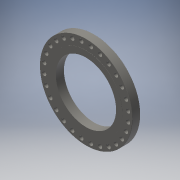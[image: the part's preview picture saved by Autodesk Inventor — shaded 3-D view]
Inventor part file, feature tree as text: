
AUTODESK INVENTOR PART (.ipt)
format: ipt  version: 2017 SP1 (Build 210196100, 196)  size: 296,960 bytes
history: native  units: in
note: dims shown in document units (in); Inventor stores cm internally (conversion verified against a paired STEP export)
features: sketch x6, extrude x4, chamfer x3, hole x2, pattern_circular x2, fillet x1, plane x1, projected_geometry x1
ambient origin geometry x8: Origin, YZ Plane, XZ Plane, XY Plane, X Axis, Y Axis, Z Axis, Center Point
bodies: Solid1 (feature_tree)
feature tree (20):
  extrude  "Extrusion: OD"  Depth=3.6875in TaperAngle=0.0deg
  extrude  "Extrusion: RF"  Depth=0.0625in TaperAngle=0.0deg
  extrude  "Extrusion: ID Large"  Depth=2.0in TaperAngle=0.0deg
  extrude  "Extrusion: ID Small"  Depth=2.0in TaperAngle=0.0deg
  hole  "Hole: Bolt"  [1 undecoded]
  chamfer  "Chamfer: Bolt hole"  Distance=11.0236in Angle=360.0deg
  pattern_circular  "Circular Pattern: Bolt hole"  Angle=45.0deg  [1 undecoded]
  chamfer  "Chamfer: OD"  Distance=0.0312in Angle=45.0deg
  chamfer  "Chamfer2"  Distance=0.0312in
  fillet  "Fillet2"  Radius=0.25in
  plane  "Work Plane1"
  hole  "Hole2"  [1 undecoded]
  pattern_circular  "Circular Pattern2"  [2 undecoded]
  sketch  "Sketch1"  dims[d0=43.0in d1=3.6875in d2=0.0in]
  sketch  "Sketch2"  dims[d3=33.75in d4=0.0625in d5=0.0in]
  sketch  "Sketch3"  dims[d6=30.0in d7=2.0in d8=0.0in]
  sketch  "Sketch4"  dims[d9=28.0in d10=2.0in d11=0.0in]
  sketch  "Sketch5"  dims[d12=39.25in d13=0.0442in]
  sketch  "Sketch6"  dims[d14=1.875in d15=0.75in d16=0.375in d17=0.25in d18=0.5635in d19=1.0in d20=0.8108in d21=11.0236in d22=360.0deg d24=0.0625in d25=0.125in d26=45.0deg d28=0.0312in d29=0.125in d30=45.0deg d31=0.0312in d32=0.25in d33=0.0625in d34=0.125in d35=45.0deg d36=1.875in d37=0.642in d38=2.0in d39=0.375in d40=0.25in d41=0.5635in d42=2.5in d43=0.8108in d44=0.7874in d45=360.0deg]
  projected_geometry  "Projected Loop1"
note: 5 required parameter values undecoded (feature->parameter linkage not recoverable at this tier; creation-order binding heuristic only, values carry confidence <= 0.55)
